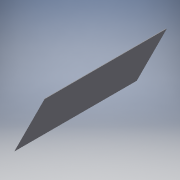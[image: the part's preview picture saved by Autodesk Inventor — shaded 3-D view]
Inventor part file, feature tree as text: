
AUTODESK INVENTOR PART (.ipt)
format: ipt  version: 2016 (Build 200138000, 138)  size: 87,552 bytes
history: native  units: mm
features: extrude x1, sketch x1
ambient origin geometry x8: Origin, YZ Plane, XZ Plane, XY Plane, X Axis, Y Axis, Z Axis, Center Point
bodies: Solid1 (feature_tree)
feature tree (2):
  extrude  "Extrusion1"  Depth=540.0mm
  sketch  "Sketch1"  dims[d0=2.0mm d1=540.0mm d2=90.0mm d3=0.0mm]
